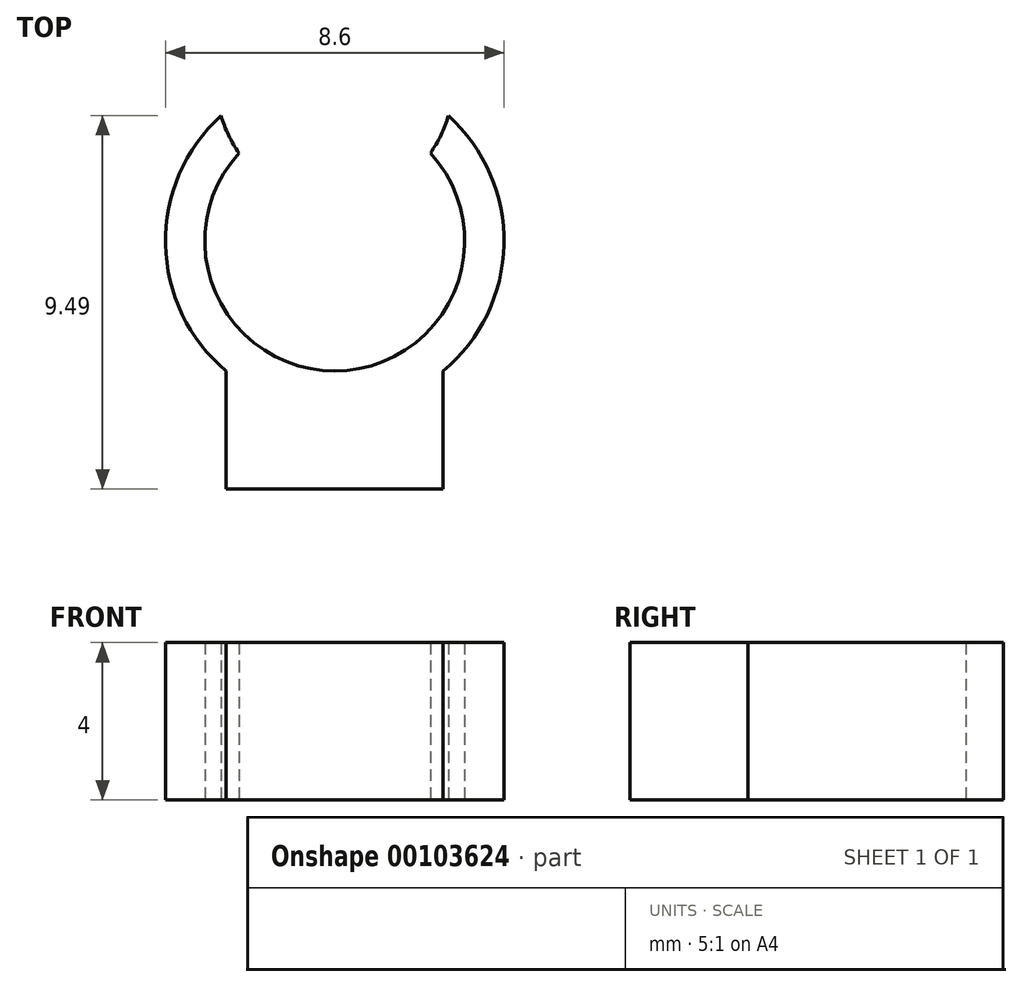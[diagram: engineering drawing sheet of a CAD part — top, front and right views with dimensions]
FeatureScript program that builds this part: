
annotation { "Feature Type Name" : "Feature", "Feature Type Description" : "" }
export const myFeature = defineFeature(function(context is Context, id is Id, definition is map)
    precondition{}
    {
        {
            var Q0;
            Q0=qCreatedBy(makeId("Top.planeOp"),FACE);
            var sketch = newSketch(context, id + "F0", { "sketchPlane" : qUnion([Q0])});
            skArc(sketch, "E0", {"start": v(-2.43, 2.24) * mm, "mid": v(0, -3.3) * mm, "end": v(2.43, 2.24) * mm});
            skArc(sketch, "E1", {"start": v(-2.89, 3.19) * mm, "mid": v(-4.3, -0.09) * mm, "end": v(-2.76, -3.3) * mm});
            skArc(sketch, "E2", {"start": v(-2.89, 3.19) * mm, "mid": v(-2.7, 2.7) * mm, "end": v(-2.43, 2.24) * mm});
            skArc(sketch, "E3.trimOffspring", {"start": v(2.43, 2.24) * mm, "mid": v(2.7, 2.7) * mm, "end": v(2.89, 3.19) * mm});
            skLineSegment(sketch, "E4.bottom", {"start": v(-2.76, -6.3) * mm, "end": v(2.76, -6.3) * mm});
            skLineSegment(sketch, "E4.top", {"start": v(-2.76, -3.3) * mm, "end": v(2.76, -3.3) * mm, "construction": true});
            skLineSegment(sketch, "E4.left", {"start": v(-2.76, -6.3) * mm, "end": v(-2.76, -3.3) * mm});
            skLineSegment(sketch, "E4.right", {"start": v(2.76, -6.3) * mm, "end": v(2.76, -3.3) * mm});
            skArc(sketch, "E5", {"start": v(-2.76, -3.3) * mm, "mid": v(0, -4.3) * mm, "end": v(2.76, -3.3) * mm, "construction": true});
            skArc(sketch, "E6", {"start": v(2.76, -3.3) * mm, "mid": v(4.3, -0.09) * mm, "end": v(2.89, 3.19) * mm});
            skSolve(sketch);
        }
        {
            var Q0;
            Q0 = qSketchRegion(id + "F0", true);
            extrude(context, id + "F1", {"entities" : qUnion([Q0]), "depth" : 4 * mm});
        }
    });
